# Revit family: IS_Connect_T9891_BIM_IT
name_source: partatom
category: Plumbing Fixtures
revit_build: Autodesk Revit 2017 (Build: 20160225_1515(x64)
units: mm (PartAtom-declared; Revit-internal decimal feet)

## family parameters
Always vertical = No
Cut with Voids When Loaded = No
OmniClass Number = 23.45.05.14.21.11
OmniClass Title = Bath/Shower Units
Part Type = Normal
Room Calculation Point = No
Round Connector Dimension = Use Diameter
Shared = No
Work Plane-Based = No

## types (2) — shared parameters
Accessori = www.idealstandard.it
AltezzaNominale = 1900 mm  [stored 6.2336 ft]
Autore = Ideal Standard
BIMobject category = Showers
BIMobject category code = sanitary-shower-screens
BIMobject main category = Sanitary
BIMobject main category code = sanitary
BOSUseNativeGeometries = 1
Brand = Ideal Standard
Brand url = http://www.idealstandard.it
Caratteristiche = Connect- PSC/155 - Porta doccia con apertura scorrevole laterale - Vetro temperato trasparente - Profilo Bianco
CodiceABarre = 8014140382706
CodiceDiPrestazione = EN
Colore = Transparente, Argento
Connessione = piombatura
Date of publishing = 2019_01_04
Description = Connect- PSC/155 - Porta doccia con apertura scorrevole laterale - Vetro temperato trasparente - Profilo Bianco
DescrizioneClassifcazioneUni2015 = Shower enclosures
Desrizione = Connect- PSC/155 - Porta doccia con apertura scorrevole laterale - Vetro temperato trasparente - Profilo Bianco
Dimensione = 1980 x 850 x 50mm
EAN code = https://8014140382706
Edition number = 1
Finitura = Transparente, Argento
Forma = Rectangolare
Garanzia = Garanzia Ideal Standard
Grado = n/s
IFC Classification = IfcSanitaryTerminal
IfcEsportaCome = FurnitureType
InformazioniDiProdotto = http://www.idealstandard.it
Installation instructions = http://www.idealstandard.it
Installazione = http://www.idealstandard.it
InstruzioniInstallazione = http://www.idealstandard.it
LarghezzaNominale = 1520 mm
LunghezzaNominale = 60 mm
Maniglia = No
Manufacturer name = Ideal Standard
Material main = Glass
Materiale = Glass
ModelloDiRiferimento = Connect- PSC/155 - Porta doccia con apertura scorrevole laterale - Vetro temperato trasparente - Profilo Bianco
NBS Reference Code = 46-35-70/332
NBS Reference Description = Shower Enclosures
NominalHeight = 1900 mm  [stored 6.2336 ft]
NominalLength = 60 mm
NominalWidth = 1520 mm
OmniClass Code = 23-31 17 00
OmniClass Description = Showers
PartiDiRicambio = http://www.idealstandard.it
PesoNetto = 21
PiattoDoccia = No
Product Guid = 0b5d40a0-3c9b-4ed4-a39c-c5ab773668c0
Product SKU = T9891
Product certification = http://www.idealstandard.it
Product data url = https://bimobject.com
Product family = Sanitary
Product group = Shower enclosures
Product name = CONNECT SL DR155U/H DR IC CLR BRT/SIL EU
Product url = http://www.idealstandard.it
QR code = http://bimobject.com
Revisione = 1
RiferimentoClassificazioneUni2015 = Pr_40_20_06_79
Size = 1980 x 850 x 50mm
Technical description = http://www.idealstandard.it
Telefono = 800 652 290
TipoDiDato = Fisso
TipoEspotazioneIfc = IfcSanitaryTerminalType
URL = http://www.idealstandard.it
Uniclass 1.4 Code = L72142
Uniclass 1.4 Description = Shower screens, curtains
Uniclass 2.0 Code = PR-35-06-79
Uniclass 2.0 Description = Shower Enclosures
Uniclass 2015 Code = Pr_40_20_06_79
Uniclass 2015 Name = Shower enclosures
UnitàDurata = anni
UnitàDurataGaranzia = anni
UnitàLineare = millimetri
UnitàMonetaria = €
UnitàSuperficie = €
UnitàVolume = millimetri
Versione = 1
VersioneClassificazioneUni2015 = 1
Youtube clip = https://www.youtube.com
zero-valued in all types: CostoDiSostituzione, DimensioneScarico, Nominal depth, Nominal height, ProfonditaNominale, SeatMaterial, SpessoreDelMateriale, SpilloverLivello, Weight Net (Kg)

## per-type parameters (varying)
| type | Model | Nome | NomeOggettoBim | NumeroDiModello |
| T9891AC - CONNECT PSC155 REV IC TRAS BIANCO EU | T9891AC | ShowerEnclosure_Concept_T9891AC_IdealStandard | ISI_IdealStandard_ShowerEnclosure_Concept_T9891AC | T9890EO |
| T9891EO - CONNECT PSC155 REV IC TRAS BRT/SL EU | T9891EO | ShowerEnclosure_Concept_T9891EO_IdealStandard | ISI_IdealStandard_ShowerEnclosure_Concept_T9891EO | T9891AC |

note: [stored X ft] marks values corroborated as IEEE doubles in the binary element streams (Revit-internal decimal feet)

## geometry (parser evidence)
native form markers: Sweep x3
no freeform markers — native parametric forms only
